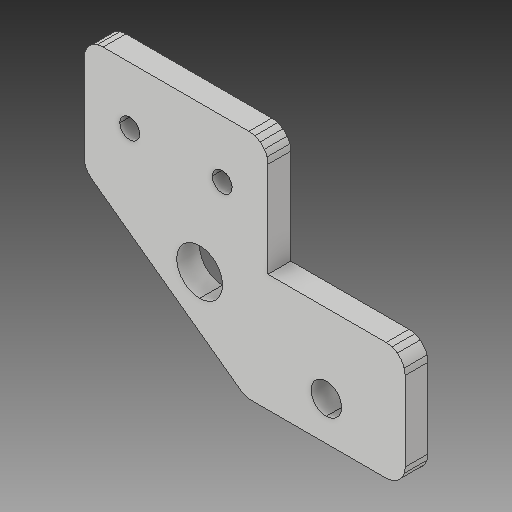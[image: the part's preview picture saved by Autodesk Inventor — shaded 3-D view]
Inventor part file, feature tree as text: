
AUTODESK INVENTOR PART (.ipt)
format: ipt  version: 2018 (Build 220112000, 112)  size: 237,056 bytes
history: native  units: mm
features: sketch x2, extrude x1, hole x1, projected_geometry x1
ambient origin geometry x8: Origin, YZ Plane, XZ Plane, XY Plane, X Axis, Y Axis, Z Axis, Center Point
bodies: Solid1 (feature_tree)
feature tree (5):
  extrude  "Extrusion1"  [1 undecoded]
  hole  "Hole1"  [1 undecoded]
  sketch  "Sketch1"  dims[d0=6.0mm d1=0.0mm]
  sketch  "Sketch2"  dims[d2=5.2mm d3=6.0mm d4=4.0mm d5=2.0mm d6=90.0deg d7=8.0mm d8=20.594885mm]
  projected_geometry  "Projected Loop1"
note: 2 required parameter values undecoded (feature->parameter linkage not recoverable at this tier; creation-order binding heuristic only, values carry confidence <= 0.55)
